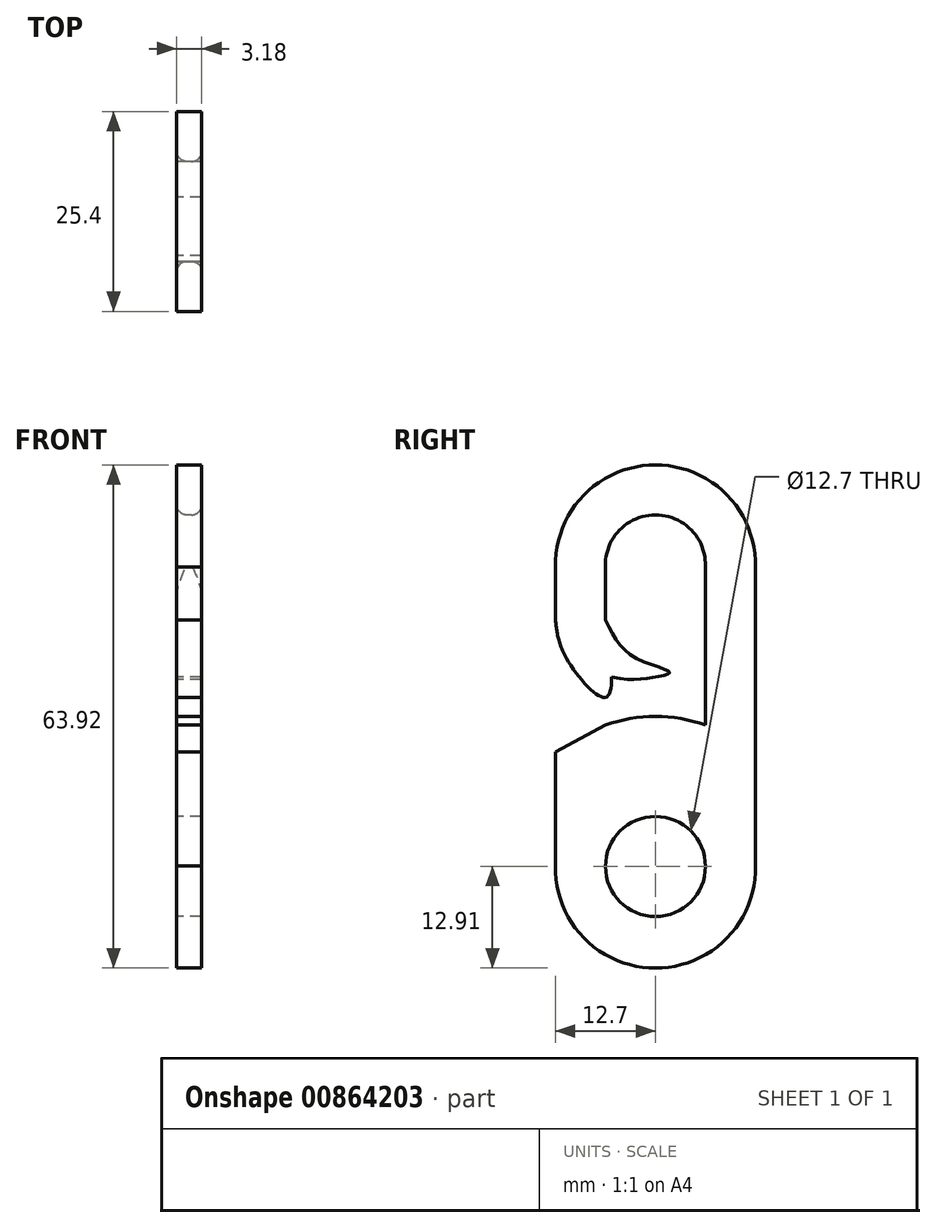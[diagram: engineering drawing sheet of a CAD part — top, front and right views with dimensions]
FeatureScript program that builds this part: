
annotation { "Feature Type Name" : "Feature", "Feature Type Description" : "" }
export const myFeature = defineFeature(function(context is Context, id is Id, definition is map)
    precondition{}
    {
        {
            var Q0;
            Q0=qCreatedBy(makeId("Right.planeOp"),FACE);
            var sketch = newSketch(context, id + "F0", { "sketchPlane" : qUnion([Q0])});
            skLineSegment(sketch, "E0.left", {"start": v(6.35, -1.09) * mm, "end": v(6.35, 19.05) * mm});
            skPoint(sketch, "E0.middle", {"position": v(0, 0) * mm});
            skArc(sketch, "E1", {"start": v(6.35, 19.05) * mm, "mid": v(0, 25.61) * mm, "end": v(-6.35, 19.05) * mm});
            skPoint(sketch, "E1.third.point", {"position": v(0, 25.61) * mm});
            skPoint(sketch, "E1.third.point.positionSnap0", {"position": v(0, 19.05) * mm});
            skPoint(sketch, "E2.MirrorP", {"position": v(0, -19.05) * mm});
            skPoint(sketch, "E3.MirrorP", {"position": v(0, -25.61) * mm});
            skPoint(sketch, "E4.MirrorCS.start.orphan", {"position": v(6.35, -19.05) * mm});
            skArc(sketch, "E5.0", {"start": v(12.7, 18.96) * mm, "mid": v(0, 31.96) * mm, "end": v(-12.7, 18.96) * mm});
            skLineSegment(sketch, "E5.1", {"start": v(12.7, -18.96) * mm, "end": v(12.7, 18.96) * mm});
            skArc(sketch, "E5.2", {"start": v(12.7, -18.96) * mm, "mid": v(0, -31.96) * mm, "end": v(-12.7, -18.96) * mm});
            skLineSegment(sketch, "E5.3", {"start": v(-12.7, -18.96) * mm, "end": v(-12.7, -4.5) * mm});
            skArc(sketch, "E6.0", {"start": v(6.35, -1.09) * mm, "mid": v(0, 0) * mm, "end": v(-6.35, -1.09) * mm});
            skPoint(sketch, "E7.MirrorC.end.orphan", {"position": v(-6.35, -19.05) * mm});
            skCircle(sketch, "E8", {"center": v(0, -19.05) * mm, "radius": 6.35 * mm});
            skLineSegment(sketch, "E9.trimOffspring", {"start": v(-12.7, 12.27) * mm, "end": v(-12.7, 18.96) * mm});
            skLineSegment(sketch, "E10.trimOffspring", {"start": v(-6.35, 12.27) * mm, "end": v(-6.35, 19.05) * mm});
            skFitSpline(sketch, "E11", {"points": [v(-12.7, 12.27) * mm, v(-11.31, 7.4) * mm, v(-6.35, 2.44) * mm, v(-6.35, 12.27) * mm], "startDerivative": vector(1.65, -15.7) * mm, "endDerivative": vector(-5.13, 36.61) * mm});
            skFitSpline(sketch, "E12", {"points": [v(-5.58, 5) * mm, v(0, 5) * mm, v(1.8, 5.6) * mm, v(-2.62, 7.5) * mm, v(-6.35, 12.27) * mm], "startDerivative": vector(25.1, -5.23) * mm, "endDerivative": vector(-10.61, 21.16) * mm});
            skFitSpline(sketch, "E13", {"points": [v(-6.35, -1.09) * mm, v(-12.7, -4.5) * mm], "startDerivative": vector(-6.35, -3.41) * mm, "endDerivative": vector(-6.35, -3.41) * mm});
            skPoint(sketch, "E14.start.orphan", {"position": v(-6.35, 5.97) * mm});
            skFitSpline(sketch, "E15", {"points": [v(-5.58, 5) * mm, v(-11.31, 7.4) * mm], "startDerivative": vector(-5.73, 2.4) * mm, "endDerivative": vector(-5.73, 2.4) * mm});
            skSolve(sketch);
        }
        {
            var Q0;
            Q0=qSketchRegion(id+"F0",true);
            extrude(context, id + "F1", {"entities" : qUnion([Q0]), "depth" : 3.17 * mm, "offsetDistance" : 25.4 * mm});
        }
        {
            var Q0;
            Q0=makeQuery(id+"F1.opExtrude","SWEPT_FACE",FACE,{"disambiguationData":[OSD([sQuery(id+"F0.wireOp",EDGE,"E1")])]});
            var Q1;
            Q1=makeQuery(id+"F1.opExtrude","CAP_EDGE",EDGE,{"disambiguationData":[OSD([sQuery(id+"F0.wireOp",EDGE,"E1")])],"isStart":false});
            fillet(context, id + "F2", {"entities" : qUnion([Q0, Q1]), "radius" : 1.27 * mm, "tangentPropagation" : true, "allowEdgeOverflow" : false});
        }
    });
